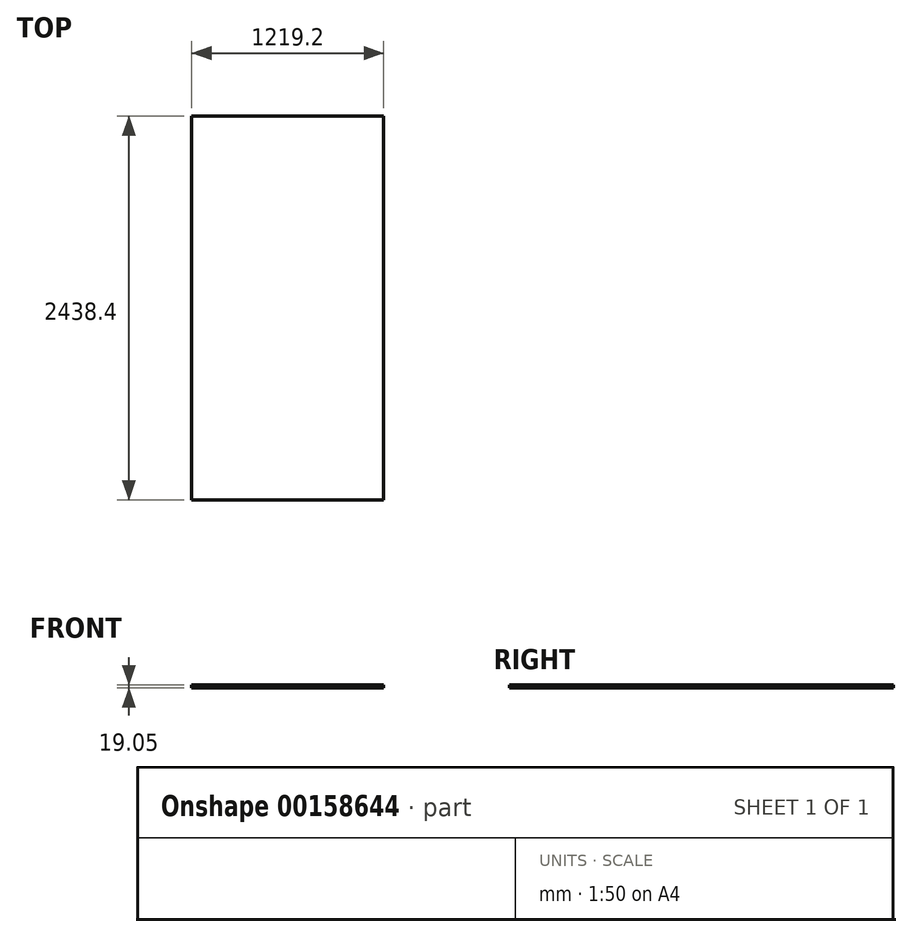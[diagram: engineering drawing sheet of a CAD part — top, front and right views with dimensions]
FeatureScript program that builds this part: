
annotation { "Feature Type Name" : "Feature", "Feature Type Description" : "" }
export const myFeature = defineFeature(function(context is Context, id is Id, definition is map)
    precondition{}
    {
        {
            var Q0;
            Q0=qCreatedBy(makeId("Top.planeOp"),FACE);
            var sketch = newSketch(context, id + "F0", { "sketchPlane" : qUnion([Q0])});
            skLineSegment(sketch, "E0.bottom", {"start": v(-609.45, 1607.56) * mm, "end": v(609.75, 1607.56) * mm});
            skLineSegment(sketch, "E0.top", {"start": v(-609.45, -830.84) * mm, "end": v(609.75, -830.84) * mm});
            skLineSegment(sketch, "E0.left", {"start": v(-609.45, 1607.56) * mm, "end": v(-609.45, -830.84) * mm});
            skLineSegment(sketch, "E0.right", {"start": v(609.75, 1607.56) * mm, "end": v(609.75, -830.84) * mm});
            skSolve(sketch);
        }
        {
            var Q0;
            Q0 = qSketchRegion(id + "F0", true);
            extrude(context, id + "F1", {"entities" : qUnion([Q0]), "depth" : 19.05 * mm});
        }
    });
